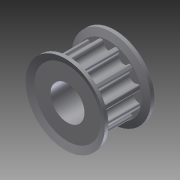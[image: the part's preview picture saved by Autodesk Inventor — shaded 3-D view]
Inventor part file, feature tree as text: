
AUTODESK INVENTOR PART (.ipt)
format: ipt  version: 2012 (Build 160160000, 160)  size: 240,128 bytes
history: native  units: in
note: dims shown in document units (in); Inventor stores cm internally (conversion verified against a paired STEP export)
features: extrude x2, sketch x1, imported_body x1
ambient origin geometry x8: Origin, YZ Plane, XZ Plane, XY Plane, X Axis, Y Axis, Z Axis, Center Point
feature tree (4):
  sketch  "Sketch1"  dims[d0=0.375in d1=0.3937in d2=0.0in d3=0.273in d4=0.0in]
  extrude  "Extrusion1"  Depth=0.3937in TaperAngle=0.0deg
  extrude  "Extrusion2"  Depth=0.273in TaperAngle=0.0deg
  imported_body  "Base1"
